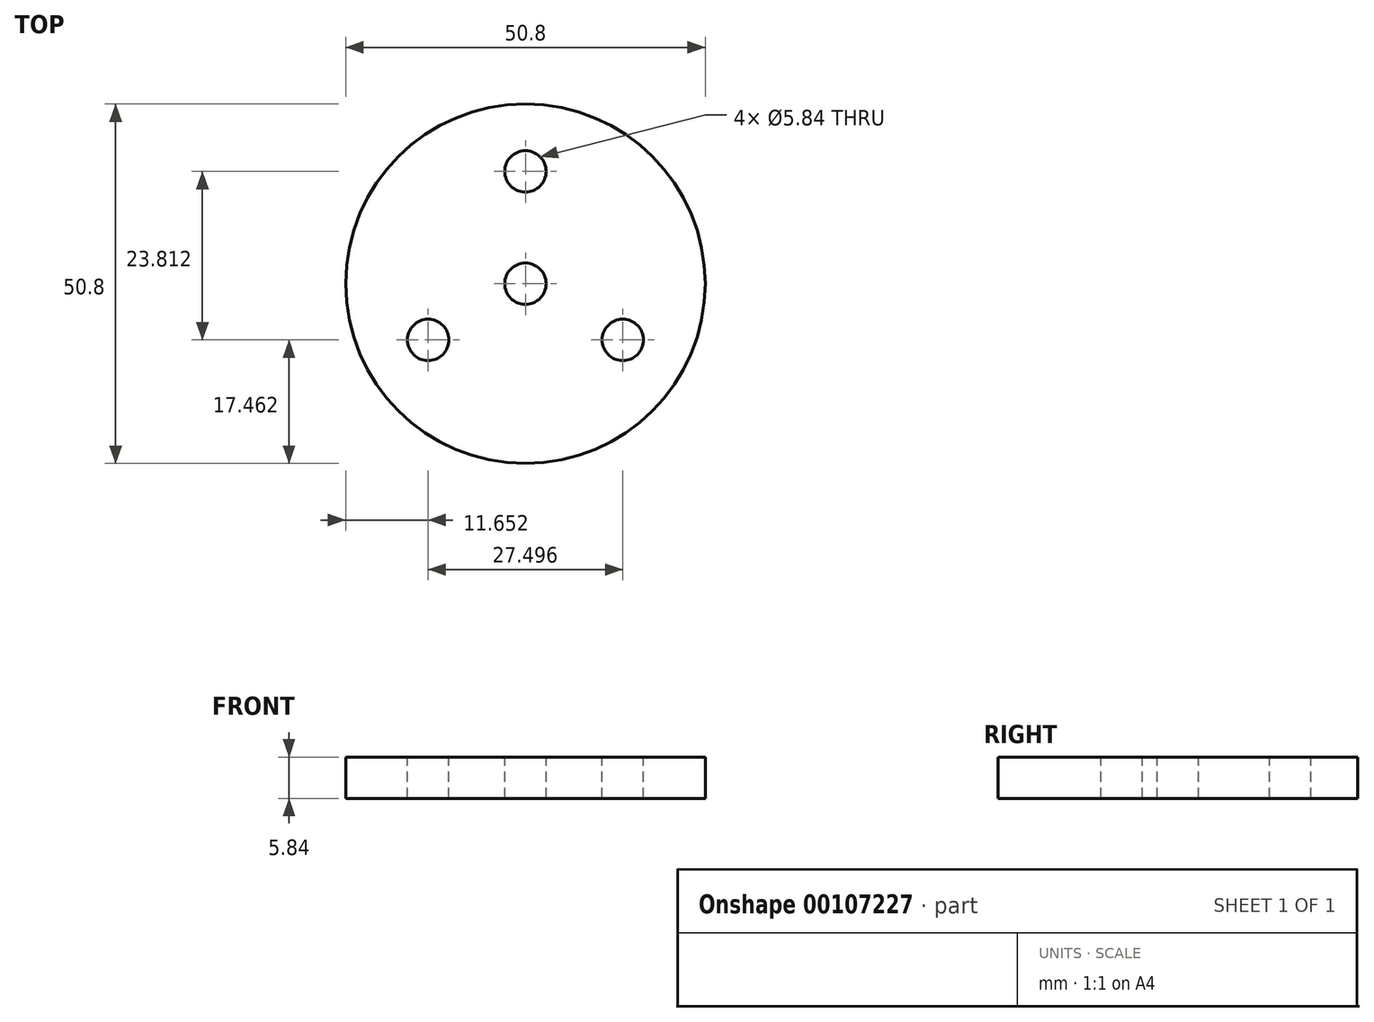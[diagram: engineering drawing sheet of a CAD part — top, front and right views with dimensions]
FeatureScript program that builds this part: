
annotation { "Feature Type Name" : "Feature", "Feature Type Description" : "" }
export const myFeature = defineFeature(function(context is Context, id is Id, definition is map)
    precondition{}
    {
        {
            var Q0;
            Q0=qCreatedBy(makeId("Top.planeOp"),FACE);
            var sketch = newSketch(context, id + "F0", { "sketchPlane" : qUnion([Q0])});
            skCircle(sketch, "E0", {"center": v(0, 0) * mm, "radius": 25.4 * mm});
            skSolve(sketch);
        }
        {
            var Q0;
            Q0=makeQuery(id+"F0.imprint","IMPRINT",FACE,{"disambiguationData":[TD([[makeQuery(id+"F0.imprint","IMPRINT",EDGE,{"derivedFrom":sQuery(id+"F0.wireOp",EDGE,"E0")}),1.0]])]});
            extrude(context, id + "F1", {"entities" : qUnion([Q0]), "depth" : 5.84 * mm});
        }
        {
            var Q0;
            Q0=makeQuery(id+"F1.opExtrude","CAP_FACE",FACE,{"disambiguationData":[OSD([sQuery(id+"F0.wireOp",EDGE,"E0")])],"isStart":false});
            var sketch = newSketch(context, id + "F2", { "sketchPlane" : qUnion([Q0])});
            skCircle(sketch, "E1", {"center": v(0, 0) * mm, "radius": 15.88 * mm, "construction": true});
            skCircle(sketch, "E2", {"center": v(0, 15.88) * mm, "radius": 2.92 * mm});
            skCircle(sketch, "E3", {"center": v(13.75, -7.94) * mm, "radius": 2.92 * mm});
            skCircle(sketch, "E4", {"center": v(-13.75, -7.94) * mm, "radius": 2.92 * mm});
            skLineSegment(sketch, "E5", {"start": v(0, 0) * mm, "end": v(0, 15.88) * mm});
            skLineSegment(sketch, "E6", {"start": v(0, 0) * mm, "end": v(-13.75, -7.94) * mm});
            skLineSegment(sketch, "E7", {"start": v(0, 0) * mm, "end": v(13.75, -7.94) * mm});
            skCircle(sketch, "E8", {"center": v(0, 0) * mm, "radius": 2.92 * mm});
            skSolve(sketch);
        }
        {
            var Q0;
            Q0=makeQuery(id+"F2.imprint","IMPRINT",FACE,{"disambiguationData":[TD([[makeQuery(id+"F2.imprint","IMPRINT",EDGE,{"derivedFrom":sQuery(id+"F2.wireOp",EDGE,"E2")}),1.0]])]});
            var Q1;
            Q1=makeQuery(id+"F2.imprint","IMPRINT",FACE,{"disambiguationData":[TD([[makeQuery(id+"F2.imprint","IMPRINT",EDGE,{"derivedFrom":sQuery(id+"F2.wireOp",EDGE,"E4")}),1.0]])]});
            var Q2;
            Q2=makeQuery(id+"F2.imprint","IMPRINT",FACE,{"disambiguationData":[TD([[makeQuery(id+"F2.imprint","IMPRINT",EDGE,{"derivedFrom":sQuery(id+"F2.wireOp",EDGE,"E3")}),1.0]])]});
            var Q3;
            {var subQ1=sQuery(id+"F2.wireOp",EDGE,"E5");var subQ3=sQuery(id+"F2.wireOp",EDGE,"E8");var subQ4=makeQuery(id+"F2.imprint","INTERSECT",VERTEX,{"derivedFrom":[subQ1,subQ3]});Q3=makeQuery(id+"F2.imprint","IMPRINT",FACE,{"disambiguationData":[TD([[makeQuery(id+"F2.imprint","IMPRINT",EDGE,{"disambiguationData":[TD([[subQ4,-1.0]])],"derivedFrom":subQ3}),1.0]])]});}
            var Q4;
            {var subQ1=sQuery(id+"F2.wireOp",EDGE,"E5");var subQ3=sQuery(id+"F2.wireOp",EDGE,"E8");var subQ4=makeQuery(id+"F2.imprint","INTERSECT",VERTEX,{"derivedFrom":[subQ1,subQ3]});Q4=makeQuery(id+"F2.imprint","IMPRINT",FACE,{"disambiguationData":[TD([[makeQuery(id+"F2.imprint","IMPRINT",EDGE,{"disambiguationData":[TD([[subQ4,1.0]])],"derivedFrom":subQ3}),1.0]])]});}
            var Q5;
            {var subQ1=sQuery(id+"F2.wireOp",EDGE,"E6");var subQ3=sQuery(id+"F2.wireOp",EDGE,"E8");var subQ4=makeQuery(id+"F2.imprint","INTERSECT",VERTEX,{"derivedFrom":[subQ1,subQ3]});Q5=makeQuery(id+"F2.imprint","IMPRINT",FACE,{"disambiguationData":[TD([[makeQuery(id+"F2.imprint","IMPRINT",EDGE,{"disambiguationData":[TD([[subQ4,-1.0]])],"derivedFrom":subQ3}),1.0]])]});}
            var Q6;
            Q6=makeQuery(id+"F1.opExtrude","CAP_FACE",FACE,{"disambiguationData":[OSD([sQuery(id+"F0.wireOp",EDGE,"E0")])],"isStart":true});
            extrude(context, id + "F3", {"entities" : qUnion([Q0, Q1, Q2, Q3, Q4, Q5]), "operationType" : NewBodyOperationType.REMOVE, "endBound" : BoundingType.UP_TO_SURFACE, "oppositeDirection" : true, "endBoundEntityFace" : qUnion([Q6]), "depth" : 25.4 * mm});
        }
    });
